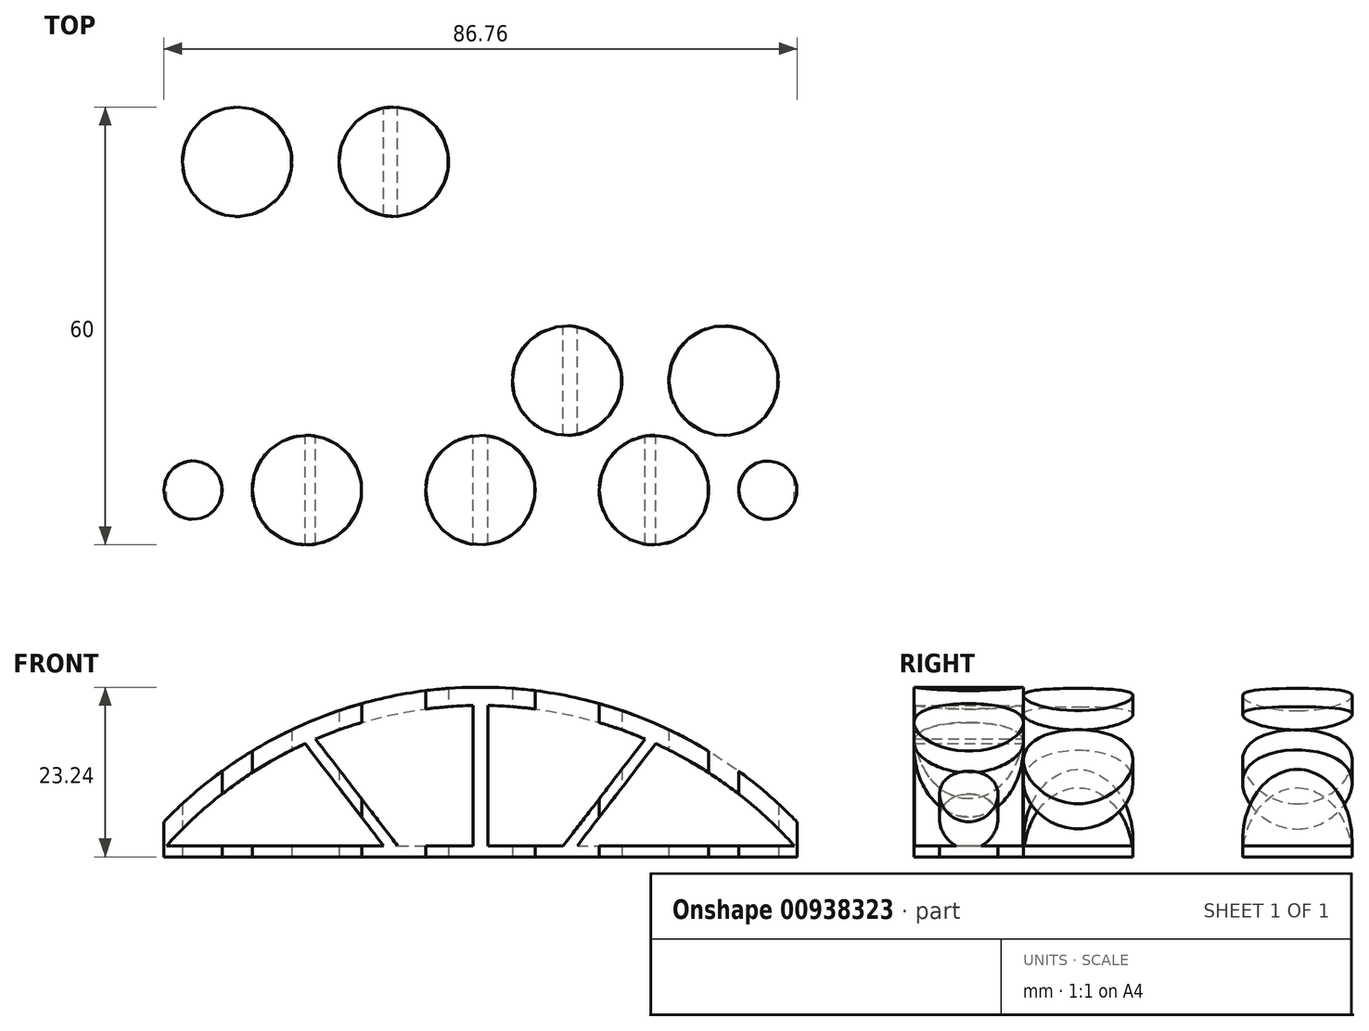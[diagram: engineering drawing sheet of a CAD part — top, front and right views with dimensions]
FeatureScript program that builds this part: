
annotation { "Feature Type Name" : "Feature", "Feature Type Description" : "" }
export const myFeature = defineFeature(function(context is Context, id is Id, definition is map)
    precondition{}
    {
        {
            var Q0;
            Q0=qCreatedBy(makeId("Front.planeOp"),FACE);
            var sketch = newSketch(context, id + "F0", { "sketchPlane" : qUnion([Q0])});
            skLineSegment(sketch, "E0", {"start": v(0, 0) * mm, "end": v(4.75, 0) * mm});
            skLineSegment(sketch, "E1", {"start": v(0, 0) * mm, "end": v(47.5, 0) * mm});
            skLineSegment(sketch, "E2", {"start": v(47.5, 0) * mm, "end": v(-47.5, 0) * mm});
            skArc(sketch, "E3", {"start": v(47.5, 0) * mm, "mid": v(0, 23.24) * mm, "end": v(-47.5, 0) * mm});
            skArc(sketch, "E4", {"start": v(43, 1.5) * mm, "mid": v(34.22, 9.48) * mm, "end": v(24, 15.5) * mm});
            skLineSegment(sketch, "E5", {"start": v(0, 1.5) * mm, "end": v(11.33, 1.5) * mm});
            skLineSegment(sketch, "E6", {"start": v(-1, 1.5) * mm, "end": v(-11.33, 1.5) * mm});
            skLineSegment(sketch, "E7", {"start": v(0, 0) * mm, "end": v(-1, 0) * mm});
            skLineSegment(sketch, "E8", {"start": v(-1, 1.5) * mm, "end": v(-1, 20.73) * mm});
            skLineSegment(sketch, "E9", {"start": v(0, 0) * mm, "end": v(1, 0) * mm});
            skLineSegment(sketch, "E10", {"start": v(1, 1.5) * mm, "end": v(1, 20.73) * mm});
            skPoint(sketch, "E11.start.orphan", {"position": v(0, 23.24) * mm});
            skArc(sketch, "E12.trimOffspring", {"start": v(-1, 20.73) * mm, "mid": v(-12, 19.47) * mm, "end": v(-22.57, 16.14) * mm});
            skLineSegment(sketch, "E13", {"start": v(13.26, 1.5) * mm, "end": v(24, 15.5) * mm});
            skLineSegment(sketch, "E14", {"start": v(11.33, 1.5) * mm, "end": v(22.57, 16.14) * mm});
            skLineSegment(sketch, "E15", {"start": v(0, 23.24) * mm, "end": v(0, 14.82) * mm});
            skLineSegment(sketch, "E16.MirrorCS", {"start": v(-11.33, 1.5) * mm, "end": v(-22.57, 16.14) * mm});
            skLineSegment(sketch, "E17.MirrorCS", {"start": v(-13.26, 1.5) * mm, "end": v(-24, 15.5) * mm});
            skArc(sketch, "E18.trimOffspring", {"start": v(-24, 15.5) * mm, "mid": v(-34.22, 9.48) * mm, "end": v(-43, 1.5) * mm});
            skLineSegment(sketch, "E19.trimOffspring", {"start": v(-13.26, 1.5) * mm, "end": v(-43, 1.5) * mm});
            skLineSegment(sketch, "E20.trimOffspring", {"start": v(13.26, 1.5) * mm, "end": v(43, 1.5) * mm});
            skArc(sketch, "E21.trimOffspring", {"start": v(22.57, 16.14) * mm, "mid": v(12, 19.47) * mm, "end": v(1, 20.73) * mm});
            skSolve(sketch);
        }
        {
            var Q0;
            Q0=makeQuery(id+"F0.imprint","IMPRINT",FACE,{"disambiguationData":[TD([[makeQuery(id+"F0.imprint","IMPRINT",EDGE,{"derivedFrom":sQuery(id+"F0.wireOp",EDGE,"E4")}),-1.0]])]});
            extrude(context, id + "F1", {"entities" : qUnion([Q0]), "depth" : 90 * mm, "offsetDistance" : 25 * mm});
        }
        {
            var Q0;
            Q0=makeQuery(id+"F1.opExtrude","SWEPT_FACE",FACE,{"disambiguationData":[OSD([sQuery(id+"F0.wireOp",EDGE,"E2"),sQuery(id+"F0.wireOp",EDGE,"E7"),sQuery(id+"F0.wireOp",EDGE,"E9")])]});
            var sketch = newSketch(context, id + "F2", { "sketchPlane" : qUnion([Q0])});
            skLineSegment(sketch, "E22", {"start": v(47.5, 45) * mm, "end": v(47.5, 90) * mm});
            skCircle(sketch, "E23", {"center": v(0, 45) * mm, "radius": 7.5 * mm});
            skCircle(sketch, "E24", {"center": v(23.75, 45) * mm, "radius": 7.5 * mm});
            skCircle(sketch, "E25", {"center": v(-23.75, 45) * mm, "radius": 7.5 * mm});
            skCircle(sketch, "E26", {"center": v(39.38, 45) * mm, "radius": 4 * mm});
            skCircle(sketch, "E27", {"center": v(-39.38, 45) * mm, "radius": 4 * mm});
            skLineSegment(sketch, "E28", {"start": v(-47.5, 45) * mm, "end": v(-47.5, 55.5) * mm});
            skLineSegment(sketch, "E29", {"start": v(-47.5, 45) * mm, "end": v(-47.5, 60) * mm});
            skCircle(sketch, "E30", {"center": v(-11.87, 60) * mm, "radius": 7.5 * mm});
            skCircle(sketch, "E31.MirrorC", {"center": v(11.87, 60) * mm, "radius": 7.5 * mm});
            skCircle(sketch, "E32", {"center": v(-33.31, 60) * mm, "radius": 7.5 * mm});
            skCircle(sketch, "E33.MirrorC", {"center": v(33.31, 60) * mm, "radius": 7.5 * mm});
            skCircle(sketch, "E34.MirrorC", {"center": v(-33.31, 30) * mm, "radius": 7.5 * mm});
            skCircle(sketch, "E35.MirrorC", {"center": v(-11.87, 30) * mm, "radius": 7.5 * mm});
            skCircle(sketch, "E36.MirrorC", {"center": v(11.88, 30) * mm, "radius": 7.5 * mm});
            skCircle(sketch, "E37.MirrorC", {"center": v(33.31, 30) * mm, "radius": 7.5 * mm});
            skCircle(sketch, "E38.MirrorC", {"center": v(-39.38, 75) * mm, "radius": 4 * mm});
            skCircle(sketch, "E39.MirrorC", {"center": v(-23.75, 75) * mm, "radius": 7.5 * mm});
            skCircle(sketch, "E40.MirrorC", {"center": v(0, 75) * mm, "radius": 7.5 * mm});
            skCircle(sketch, "E41.MirrorC", {"center": v(23.75, 75) * mm, "radius": 7.5 * mm});
            skCircle(sketch, "E42.MirrorC", {"center": v(39.38, 75) * mm, "radius": 4 * mm});
            skCircle(sketch, "E43.MirrorC", {"center": v(-39.37, 15) * mm, "radius": 4 * mm});
            skCircle(sketch, "E44.MirrorC", {"center": v(-23.75, 15) * mm, "radius": 7.5 * mm});
            skCircle(sketch, "E45.MirrorC", {"center": v(0, 15) * mm, "radius": 7.5 * mm});
            skCircle(sketch, "E46.MirrorC", {"center": v(23.75, 15) * mm, "radius": 7.5 * mm});
            skCircle(sketch, "E47.MirrorC", {"center": v(39.38, 15) * mm, "radius": 4 * mm});
            skSolve(sketch);
        }
        {
            var Q0;
            Q0=makeQuery(id+"F2.imprint","IMPRINT",FACE,{"disambiguationData":[TD([[makeQuery(id+"F2.imprint","IMPRINT",EDGE,{"derivedFrom":sQuery(id+"F2.wireOp",EDGE,"E38.MirrorC")}),-1.0]])]});
            var Q1;
            Q1=makeQuery(id+"F2.imprint","IMPRINT",FACE,{"disambiguationData":[TD([[makeQuery(id+"F2.imprint","IMPRINT",EDGE,{"derivedFrom":sQuery(id+"F2.wireOp",EDGE,"E39.MirrorC")}),-1.0]])]});
            var Q2;
            Q2=makeQuery(id+"F2.imprint","IMPRINT",FACE,{"disambiguationData":[TD([[makeQuery(id+"F2.imprint","IMPRINT",EDGE,{"derivedFrom":sQuery(id+"F2.wireOp",EDGE,"E40.MirrorC")}),-1.0]])]});
            var Q3;
            Q3=makeQuery(id+"F2.imprint","IMPRINT",FACE,{"disambiguationData":[TD([[makeQuery(id+"F2.imprint","IMPRINT",EDGE,{"derivedFrom":sQuery(id+"F2.wireOp",EDGE,"E41.MirrorC")}),-1.0]])]});
            var Q4;
            Q4=makeQuery(id+"F2.imprint","IMPRINT",FACE,{"disambiguationData":[TD([[makeQuery(id+"F2.imprint","IMPRINT",EDGE,{"derivedFrom":sQuery(id+"F2.wireOp",EDGE,"E42.MirrorC")}),-1.0]])]});
            var Q5;
            Q5=makeQuery(id+"F2.imprint","IMPRINT",FACE,{"disambiguationData":[TD([[makeQuery(id+"F2.imprint","IMPRINT",EDGE,{"derivedFrom":sQuery(id+"F2.wireOp",EDGE,"E32")}),1.0]])]});
            var Q6;
            Q6=makeQuery(id+"F2.imprint","IMPRINT",FACE,{"disambiguationData":[TD([[makeQuery(id+"F2.imprint","IMPRINT",EDGE,{"derivedFrom":sQuery(id+"F2.wireOp",EDGE,"E30")}),1.0]])]});
            var Q7;
            Q7=makeQuery(id+"F2.imprint","IMPRINT",FACE,{"disambiguationData":[TD([[makeQuery(id+"F2.imprint","IMPRINT",EDGE,{"derivedFrom":sQuery(id+"F2.wireOp",EDGE,"E31.MirrorC")}),-1.0]])]});
            var Q8;
            Q8=makeQuery(id+"F2.imprint","IMPRINT",FACE,{"disambiguationData":[TD([[makeQuery(id+"F2.imprint","IMPRINT",EDGE,{"derivedFrom":sQuery(id+"F2.wireOp",EDGE,"E33.MirrorC")}),-1.0]])]});
            var Q9;
            Q9=makeQuery(id+"F2.imprint","IMPRINT",FACE,{"disambiguationData":[TD([[makeQuery(id+"F2.imprint","IMPRINT",EDGE,{"derivedFrom":sQuery(id+"F2.wireOp",EDGE,"E26")}),1.0]])]});
            var Q10;
            Q10=makeQuery(id+"F2.imprint","IMPRINT",FACE,{"disambiguationData":[TD([[makeQuery(id+"F2.imprint","IMPRINT",EDGE,{"derivedFrom":sQuery(id+"F2.wireOp",EDGE,"E24")}),1.0]])]});
            var Q11;
            Q11=makeQuery(id+"F2.imprint","IMPRINT",FACE,{"disambiguationData":[TD([[makeQuery(id+"F2.imprint","IMPRINT",EDGE,{"derivedFrom":sQuery(id+"F2.wireOp",EDGE,"E23")}),1.0]])]});
            var Q12;
            Q12=makeQuery(id+"F2.imprint","IMPRINT",FACE,{"disambiguationData":[TD([[makeQuery(id+"F2.imprint","IMPRINT",EDGE,{"derivedFrom":sQuery(id+"F2.wireOp",EDGE,"E25")}),1.0]])]});
            var Q13;
            Q13=makeQuery(id+"F2.imprint","IMPRINT",FACE,{"disambiguationData":[TD([[makeQuery(id+"F2.imprint","IMPRINT",EDGE,{"derivedFrom":sQuery(id+"F2.wireOp",EDGE,"E27")}),1.0]])]});
            var Q14;
            Q14=makeQuery(id+"F2.imprint","IMPRINT",FACE,{"disambiguationData":[TD([[makeQuery(id+"F2.imprint","IMPRINT",EDGE,{"derivedFrom":sQuery(id+"F2.wireOp",EDGE,"E34.MirrorC")}),-1.0]])]});
            var Q15;
            Q15=makeQuery(id+"F2.imprint","IMPRINT",FACE,{"disambiguationData":[TD([[makeQuery(id+"F2.imprint","IMPRINT",EDGE,{"derivedFrom":sQuery(id+"F2.wireOp",EDGE,"E35.MirrorC")}),-1.0]])]});
            var Q16;
            Q16=makeQuery(id+"F2.imprint","IMPRINT",FACE,{"disambiguationData":[TD([[makeQuery(id+"F2.imprint","IMPRINT",EDGE,{"derivedFrom":sQuery(id+"F2.wireOp",EDGE,"E36.MirrorC")}),1.0]])]});
            var Q17;
            Q17=makeQuery(id+"F2.imprint","IMPRINT",FACE,{"disambiguationData":[TD([[makeQuery(id+"F2.imprint","IMPRINT",EDGE,{"derivedFrom":sQuery(id+"F2.wireOp",EDGE,"E37.MirrorC")}),1.0]])]});
            var Q18;
            Q18=makeQuery(id+"F2.imprint","IMPRINT",FACE,{"disambiguationData":[TD([[makeQuery(id+"F2.imprint","IMPRINT",EDGE,{"derivedFrom":sQuery(id+"F2.wireOp",EDGE,"E47.MirrorC")}),1.0]])]});
            var Q19;
            Q19=makeQuery(id+"F2.imprint","IMPRINT",FACE,{"disambiguationData":[TD([[makeQuery(id+"F2.imprint","IMPRINT",EDGE,{"derivedFrom":sQuery(id+"F2.wireOp",EDGE,"E46.MirrorC")}),1.0]])]});
            var Q20;
            Q20=makeQuery(id+"F2.imprint","IMPRINT",FACE,{"disambiguationData":[TD([[makeQuery(id+"F2.imprint","IMPRINT",EDGE,{"derivedFrom":sQuery(id+"F2.wireOp",EDGE,"E45.MirrorC")}),1.0]])]});
            var Q21;
            Q21=makeQuery(id+"F2.imprint","IMPRINT",FACE,{"disambiguationData":[TD([[makeQuery(id+"F2.imprint","IMPRINT",EDGE,{"derivedFrom":sQuery(id+"F2.wireOp",EDGE,"E44.MirrorC")}),1.0]])]});
            var Q22;
            Q22=makeQuery(id+"F2.imprint","IMPRINT",FACE,{"disambiguationData":[TD([[makeQuery(id+"F2.imprint","IMPRINT",EDGE,{"derivedFrom":sQuery(id+"F2.wireOp",EDGE,"E43.MirrorC")}),1.0]])]});
            extrude(context, id + "F3", {"entities" : qUnion([Q0, Q1, Q2, Q3, Q4, Q5, Q6, Q7, Q8, Q9, Q10, Q11, Q12, Q13, Q14, Q15, Q16, Q17, Q18, Q19, Q20, Q21, Q22]), "operationType" : NewBodyOperationType.REMOVE, "oppositeDirection" : true, "depth" : 30 * mm, "offsetDistance" : 25 * mm});
        }
    });
